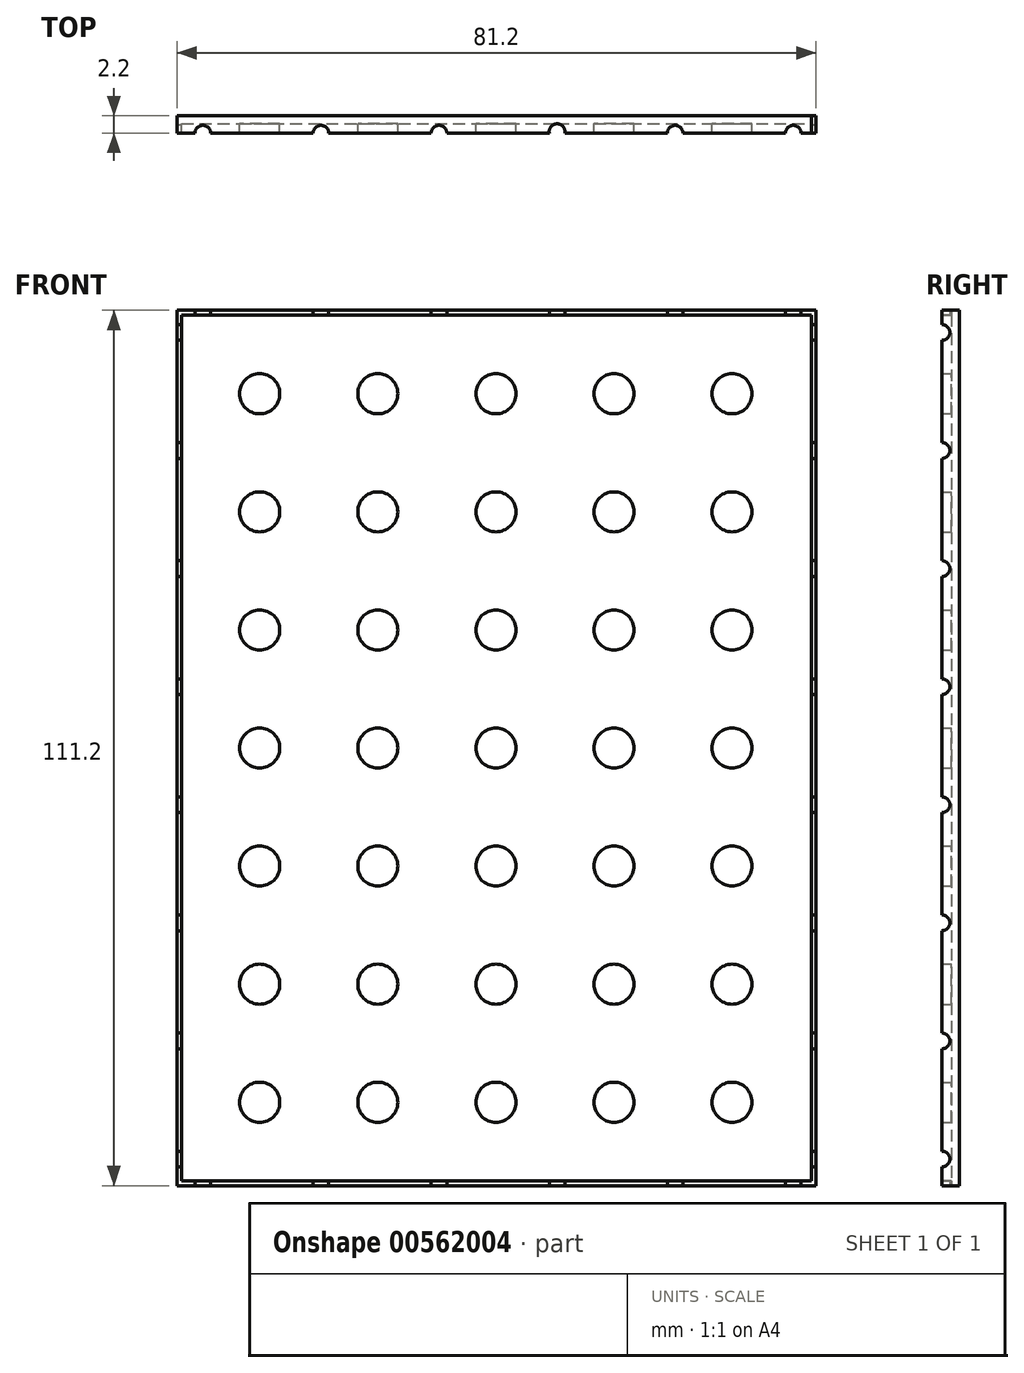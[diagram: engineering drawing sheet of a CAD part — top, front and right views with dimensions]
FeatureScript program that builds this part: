
annotation { "Feature Type Name" : "Feature", "Feature Type Description" : "" }
export const myFeature = defineFeature(function(context is Context, id is Id, definition is map)
    precondition{}
    {
        {
            var Q0;
            Q0=qCreatedBy(makeId("Front.planeOp"),FACE);
            var sketch = newSketch(context, id + "F0", { "sketchPlane" : qUnion([Q0])});
            skLineSegment(sketch, "E0.bottom", {"start": v(-40, 55) * mm, "end": v(40, 55) * mm});
            skLineSegment(sketch, "E0.top", {"start": v(-40, -55) * mm, "end": v(40, -55) * mm});
            skLineSegment(sketch, "E0.left", {"start": v(-40, 55) * mm, "end": v(-40, -55) * mm});
            skLineSegment(sketch, "E0.right", {"start": v(40, 55) * mm, "end": v(40, -55) * mm});
            skSolve(sketch);
        }
        {
            var Q0;
            Q0 = qSketchRegion(id + "F0", true);
            extrude(context, id + "F1", {"entities" : qUnion([Q0]), "depth" : 1 * mm, "offsetDistance" : 25 * mm});
        }
        {
            var Q0;
            Q0=makeQuery(id+"F0.imprint","IMPRINT",FACE,{"disambiguationData":[TD([[makeQuery(id+"F0.imprint","IMPRINT",EDGE,{"derivedFrom":sQuery(id+"F0.wireOp",EDGE,"E0.bottom")}),-1.0]])]});
            var sketch = newSketch(context, id + "F2", { "sketchPlane" : qUnion([Q0])});
            skCircle(sketch, "E1", {"center": v(-30.07, 45) * mm, "radius": 2.54 * mm});
            skCircle(sketch, "E2", {"center": v(-15.07, 45) * mm, "radius": 2.54 * mm});
            skCircle(sketch, "E3", {"center": v(-0.07, 45) * mm, "radius": 2.54 * mm});
            skCircle(sketch, "E4", {"center": v(14.93, 45) * mm, "radius": 2.54 * mm});
            skCircle(sketch, "E5", {"center": v(29.93, 45) * mm, "radius": 2.54 * mm});
            skCircle(sketch, "E6", {"center": v(-30.07, 30) * mm, "radius": 2.54 * mm});
            skCircle(sketch, "E7", {"center": v(-15.07, 30) * mm, "radius": 2.54 * mm});
            skCircle(sketch, "E8", {"center": v(-0.07, 30) * mm, "radius": 2.54 * mm});
            skCircle(sketch, "E9", {"center": v(14.93, 30) * mm, "radius": 2.54 * mm});
            skCircle(sketch, "E10", {"center": v(29.93, 30) * mm, "radius": 2.54 * mm});
            skCircle(sketch, "E11", {"center": v(-30.07, 15) * mm, "radius": 2.54 * mm});
            skCircle(sketch, "E12", {"center": v(-15.07, 15) * mm, "radius": 2.54 * mm});
            skCircle(sketch, "E13", {"center": v(-0.07, 15) * mm, "radius": 2.54 * mm});
            skCircle(sketch, "E14", {"center": v(14.93, 15) * mm, "radius": 2.54 * mm});
            skCircle(sketch, "E15", {"center": v(29.93, 15) * mm, "radius": 2.54 * mm});
            skCircle(sketch, "E16", {"center": v(-30.07, 0) * mm, "radius": 2.54 * mm});
            skCircle(sketch, "E17", {"center": v(-15.07, 0) * mm, "radius": 2.54 * mm});
            skCircle(sketch, "E18", {"center": v(-0.07, 0) * mm, "radius": 2.54 * mm});
            skCircle(sketch, "E19", {"center": v(14.93, 0) * mm, "radius": 2.54 * mm});
            skCircle(sketch, "E20", {"center": v(29.93, 0) * mm, "radius": 2.54 * mm});
            skCircle(sketch, "E21", {"center": v(-30.07, -15) * mm, "radius": 2.54 * mm});
            skCircle(sketch, "E22", {"center": v(-15.07, -15) * mm, "radius": 2.54 * mm});
            skCircle(sketch, "E23", {"center": v(-0.07, -15) * mm, "radius": 2.54 * mm});
            skCircle(sketch, "E24", {"center": v(14.93, -15) * mm, "radius": 2.54 * mm});
            skCircle(sketch, "E25", {"center": v(29.93, -15) * mm, "radius": 2.54 * mm});
            skCircle(sketch, "E26", {"center": v(-30.07, -30) * mm, "radius": 2.54 * mm});
            skCircle(sketch, "E27", {"center": v(-15.07, -30) * mm, "radius": 2.54 * mm});
            skCircle(sketch, "E28", {"center": v(-0.07, -30) * mm, "radius": 2.54 * mm});
            skCircle(sketch, "E29", {"center": v(14.93, -30) * mm, "radius": 2.54 * mm});
            skCircle(sketch, "E30", {"center": v(29.93, -30) * mm, "radius": 2.54 * mm});
            skCircle(sketch, "E31", {"center": v(-30.07, -45) * mm, "radius": 2.54 * mm});
            skCircle(sketch, "E32", {"center": v(-15.07, -45) * mm, "radius": 2.54 * mm});
            skCircle(sketch, "E33", {"center": v(-0.07, -45) * mm, "radius": 2.54 * mm});
            skCircle(sketch, "E34", {"center": v(14.93, -45) * mm, "radius": 2.54 * mm});
            skCircle(sketch, "E35", {"center": v(29.93, -45) * mm, "radius": 2.54 * mm});
            skSolve(sketch);
        }
        {
            var Q0;
            Q0 = qSketchRegion(id + "F2", true);
            extrude(context, id + "F3", {"entities" : qUnion([Q0]), "operationType" : NewBodyOperationType.ADD, "depth" : 2.2 * mm, "offsetDistance" : 25 * mm});
        }
        {
            var Q0;
            Q0=qCreatedBy(makeId("Front.planeOp"),FACE);
            var sketch = newSketch(context, id + "F4", { "sketchPlane" : qUnion([Q0])});
            skLineSegment(sketch, "E36.bottom", {"start": v(-40.6, 55.6) * mm, "end": v(-40, 55.6) * mm});
            skLineSegment(sketch, "E36.top", {"start": v(-40.6, -55.6) * mm, "end": v(-40, -55.6) * mm});
            skLineSegment(sketch, "E36.left", {"start": v(-40.6, 55.6) * mm, "end": v(-40.6, -55.6) * mm});
            skLineSegment(sketch, "E36.right", {"start": v(-40, 55.6) * mm, "end": v(-40, -55.6) * mm});
            skLineSegment(sketch, "E37.bottom", {"start": v(40, 55.6) * mm, "end": v(40.6, 55.6) * mm});
            skLineSegment(sketch, "E37.top", {"start": v(40, -55.6) * mm, "end": v(40.6, -55.6) * mm});
            skLineSegment(sketch, "E37.left", {"start": v(40, 55.6) * mm, "end": v(40, -55.6) * mm});
            skLineSegment(sketch, "E37.right", {"start": v(40.6, 55.6) * mm, "end": v(40.6, -55.6) * mm});
            skLineSegment(sketch, "E38.bottom", {"start": v(-40, -55.6) * mm, "end": v(40, -55.6) * mm});
            skLineSegment(sketch, "E38.top", {"start": v(-40, -55) * mm, "end": v(40, -55) * mm});
            skLineSegment(sketch, "E38.left", {"start": v(-40, -55.6) * mm, "end": v(-40, -55) * mm});
            skLineSegment(sketch, "E38.right", {"start": v(40, -55.6) * mm, "end": v(40, -55) * mm});
            skLineSegment(sketch, "E39.top", {"start": v(-40, 55) * mm, "end": v(-10.75, 55) * mm});
            skLineSegment(sketch, "E40.top", {"start": v(40, 55) * mm, "end": v(40.6, 55) * mm});
            skLineSegment(sketch, "E41.bottom", {"start": v(-40, 55) * mm, "end": v(40, 55) * mm});
            skLineSegment(sketch, "E41.top", {"start": v(-40, 55.6) * mm, "end": v(40, 55.6) * mm});
            skLineSegment(sketch, "E41.left", {"start": v(-40, 55) * mm, "end": v(-40, 55.6) * mm});
            skLineSegment(sketch, "E41.right", {"start": v(40, 55) * mm, "end": v(40, 55.6) * mm});
            skSolve(sketch);
        }
        {
            var Q0;
            Q0=makeQuery(id+"F4.imprint","IMPRINT",FACE,{"disambiguationData":[TD([[makeQuery(id+"F4.imprint","IMPRINT",EDGE,{"derivedFrom":sQuery(id+"F4.wireOp",EDGE,"E36.bottom")}),-1.0]])]});
            var Q1;
            {var subQ0=sQuery(id+"F4.wireOp",EDGE,"E41.top");Q1=makeQuery(id+"F4.imprint","IMPRINT",FACE,{"disambiguationData":[TD([[makeQuery(id+"F4.imprint","IMPRINT",EDGE,{"derivedFrom":subQ0}),-1.0]])]});}
            var Q2;
            {var subQ0=sQuery(id+"F4.wireOp",EDGE,"E37.right");var subQ1=sQuery(id+"F4.wireOp",EDGE,"E37.bottom");var subQ2=makeQuery(id+"F4.imprint","INTERSECT",VERTEX,{"derivedFrom":[subQ1,subQ0]});Q2=makeQuery(id+"F4.imprint","IMPRINT",FACE,{"disambiguationData":[TD([[makeQuery(id+"F4.imprint","IMPRINT",EDGE,{"disambiguationData":[TD([[subQ2,1.0]])],"derivedFrom":subQ1}),-1.0]])]});}
            var Q3;
            {var subQ0=sQuery(id+"F4.wireOp",EDGE,"E37.left");var subQ1=sQuery(id+"F4.wireOp",EDGE,"E37.bottom");var subQ2=makeQuery(id+"F4.imprint","INTERSECT",VERTEX,{"derivedFrom":[subQ1,subQ0]});Q3=makeQuery(id+"F4.imprint","IMPRINT",FACE,{"disambiguationData":[TD([[makeQuery(id+"F4.imprint","IMPRINT",EDGE,{"disambiguationData":[TD([[subQ2,-1.0]])],"derivedFrom":subQ1}),-1.0]])]});}
            var Q4;
            {var subQ2=sQuery(id+"F4.wireOp",EDGE,"E37.top");Q4=makeQuery(id+"F4.imprint","IMPRINT",FACE,{"disambiguationData":[TD([[makeQuery(id+"F4.imprint","IMPRINT",EDGE,{"derivedFrom":subQ2}),1.0]])]});}
            extrude(context, id + "F5", {"entities" : qUnion([Q0, Q1, Q2, Q3, Q4]), "operationType" : NewBodyOperationType.ADD, "depth" : 2.2 * mm, "offsetDistance" : 25 * mm});
        }
        {
            var Q0;
            Q0 = qSketchRegion(id + "F4", true);
            extrude(context, id + "F6", {"entities" : qUnion([Q0]), "operationType" : NewBodyOperationType.ADD, "depth" : 2.2 * mm, "offsetDistance" : 25 * mm});
        }
        {
            var Q0;
            {var subQ0=sQuery(id+"F4.wireOp",EDGE,"E37.top");var subQ1=sQuery(id+"F4.wireOp",EDGE,"E36.top");Q0=makeQuery(id+"F6.boolean.opBoolean","MERGE",FACE,{"derivedFrom":[makeQuery(id+"F5.opExtrude","SWEPT_FACE",FACE,{"disambiguationData":[OSD([subQ1])]}),makeQuery(id+"F5.opExtrude","SWEPT_FACE",FACE,{"disambiguationData":[OSD([subQ0])]}),makeQuery(id+"F6.opExtrude","SWEPT_FACE",FACE,{"disambiguationData":[OSD([subQ1,subQ0,sQuery(id+"F4.wireOp",EDGE,"E38.bottom")])]})]});}
            var sketch = newSketch(context, id + "F7", { "sketchPlane" : qUnion([Q0])});
            skCircle(sketch, "E42", {"center": v(7.7, 2) * mm, "radius": 1 * mm});
            skCircle(sketch, "E43", {"center": v(-37.3, 2.2) * mm, "radius": 1 * mm});
            skCircle(sketch, "E44", {"center": v(-7.3, 2.2) * mm, "radius": 1 * mm});
            skCircle(sketch, "E45", {"center": v(-22.3, 2.2) * mm, "radius": 1 * mm});
            skCircle(sketch, "E46", {"center": v(37.7, 2.2) * mm, "radius": 1 * mm});
            skCircle(sketch, "E47", {"center": v(22.7, 2.2) * mm, "radius": 1 * mm});
            skSolve(sketch);
        }
        {
            var Q0;
            Q0 = qSketchRegion(id + "F7", true);
            extrude(context, id + "F8", {"entities" : qUnion([Q0]), "operationType" : NewBodyOperationType.REMOVE, "endBound" : BoundingType.THROUGH_ALL, "oppositeDirection" : true, "depth" : 1 * mm, "offsetDistance" : 25 * mm});
        }
        {
            var Q0;
            Q0=makeQuery(id+"F5.opExtrude","SWEPT_FACE",FACE,{"disambiguationData":[OSD([sQuery(id+"F4.wireOp",EDGE,"E36.left")])]});
            var sketch = newSketch(context, id + "F9", { "sketchPlane" : qUnion([Q0])});
            skCircle(sketch, "E48", {"center": v(2.2, 52.79) * mm, "radius": 1 * mm});
            skCircle(sketch, "E49", {"center": v(2.2, 37.79) * mm, "radius": 1 * mm});
            skCircle(sketch, "E50", {"center": v(2.2, 22.79) * mm, "radius": 1 * mm});
            skCircle(sketch, "E51", {"center": v(2.2, 7.79) * mm, "radius": 1 * mm});
            skCircle(sketch, "E52", {"center": v(2.2, -7.21) * mm, "radius": 1 * mm});
            skCircle(sketch, "E53", {"center": v(2.2, -22.21) * mm, "radius": 1 * mm});
            skCircle(sketch, "E54", {"center": v(2.2, -37.21) * mm, "radius": 1 * mm});
            skCircle(sketch, "E55", {"center": v(2.2, -52.21) * mm, "radius": 1 * mm});
            skSolve(sketch);
        }
        {
            var Q0;
            Q0 = qSketchRegion(id + "F9", true);
            extrude(context, id + "F10", {"entities" : qUnion([Q0]), "operationType" : NewBodyOperationType.REMOVE, "endBound" : BoundingType.THROUGH_ALL, "oppositeDirection" : true, "depth" : 25 * mm, "offsetDistance" : 25 * mm});
        }
    });
